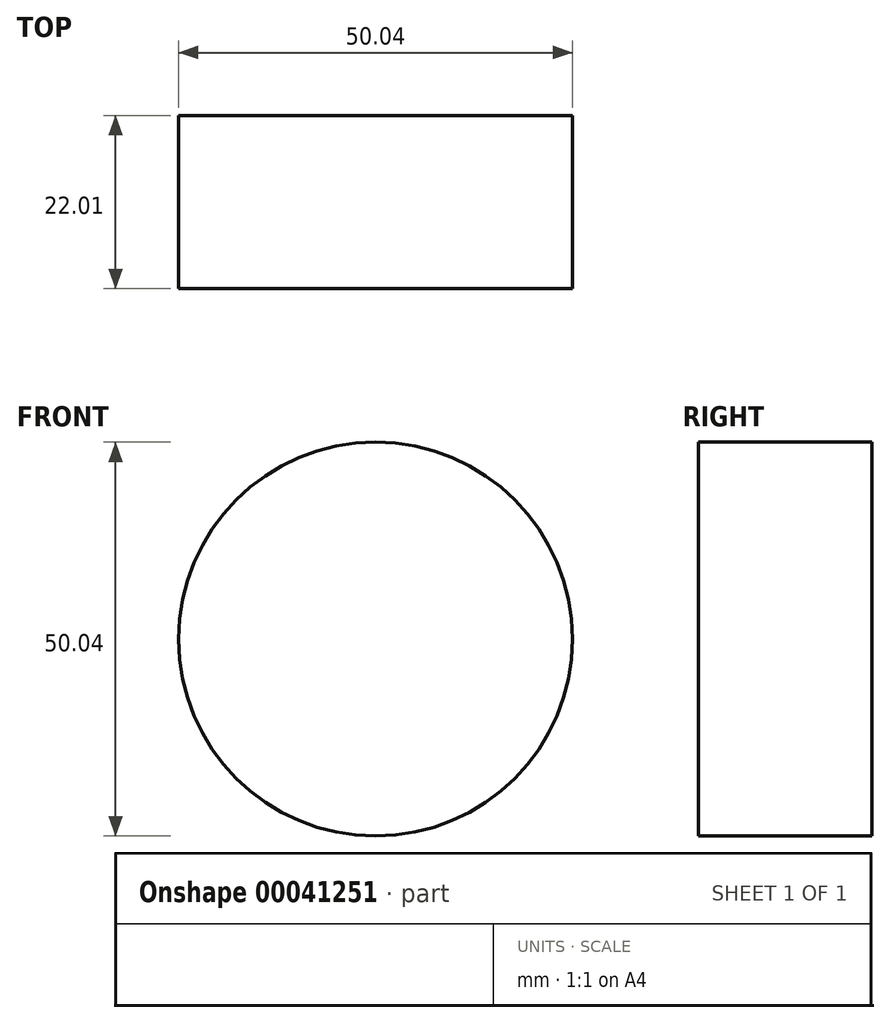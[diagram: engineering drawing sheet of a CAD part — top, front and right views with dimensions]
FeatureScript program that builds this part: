
annotation { "Feature Type Name" : "Feature", "Feature Type Description" : "" }
export const myFeature = defineFeature(function(context is Context, id is Id, definition is map)
    precondition{}
    {
        {
            var Q0;
            Q0=qCreatedBy(makeId("Front.planeOp"),FACE);
            var sketch = newSketch(context, id + "F0", { "sketchPlane" : qUnion([Q0])});
            skCircle(sketch, "E0", {"center": v(0, 0) * mm, "radius": 25.02 * mm});
            skSolve(sketch);
        }
        {
            var Q0;
            Q0=makeQuery(id+"F0.imprint","IMPRINT",FACE,{"disambiguationData":[TD([[makeQuery(id+"F0.imprint","IMPRINT",EDGE,{"derivedFrom":sQuery(id+"F0.wireOp",EDGE,"E0")}),1.0]])]});
            extrude(context, id + "F1", {"entities" : qUnion([Q0]), "depth" : 22.01 * mm});
        }
    });
